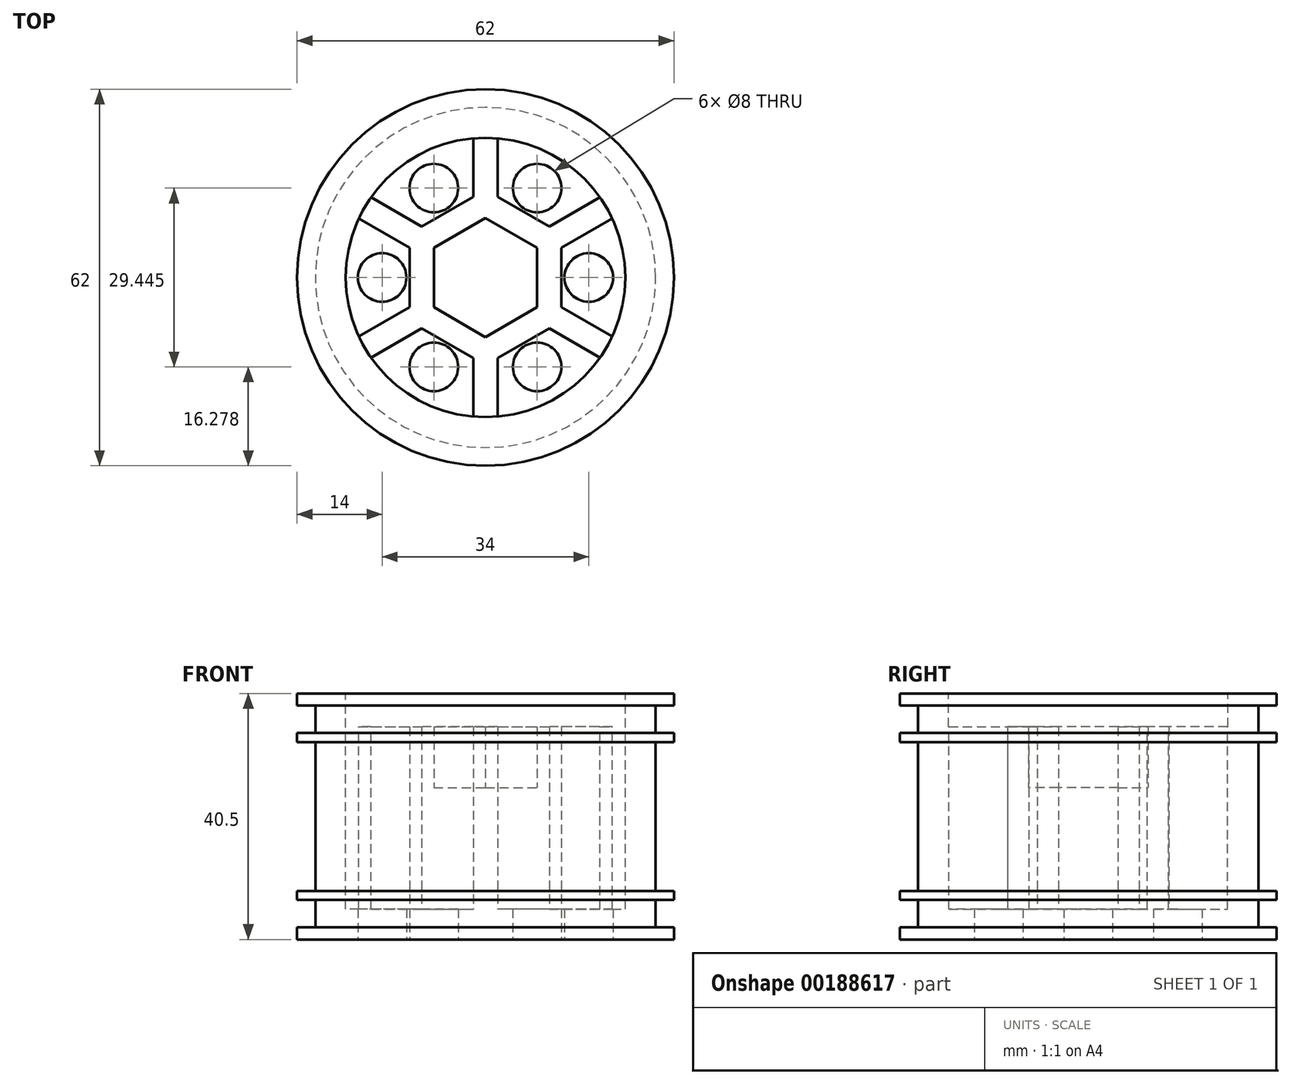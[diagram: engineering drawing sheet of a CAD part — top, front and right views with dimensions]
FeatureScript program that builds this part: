
annotation { "Feature Type Name" : "Feature", "Feature Type Description" : "" }
export const myFeature = defineFeature(function(context is Context, id is Id, definition is map)
    precondition{}
    {
        {
            var Q0;
            Q0=qCreatedBy(makeId("Front.planeOp"),FACE);
            var sketch = newSketch(context, id + "F0", { "sketchPlane" : qUnion([Q0])});
            skLineSegment(sketch, "E0", {"start": v(0, 0) * mm, "end": v(31, 0) * mm});
            skLineSegment(sketch, "E1", {"start": v(31, 0) * mm, "end": v(31, 2) * mm});
            skLineSegment(sketch, "E2", {"start": v(31, 40.5) * mm, "end": v(23, 40.5) * mm});
            skLineSegment(sketch, "E3", {"start": v(0, 5) * mm, "end": v(0, 0) * mm});
            skLineSegment(sketch, "E4.bottom", {"start": v(31, 2) * mm, "end": v(28, 2) * mm});
            skLineSegment(sketch, "E4.top", {"start": v(31, 6.5) * mm, "end": v(28, 6.5) * mm});
            skLineSegment(sketch, "E4.right", {"start": v(28, 2) * mm, "end": v(28, 6.5) * mm});
            skLineSegment(sketch, "E5.bottom", {"start": v(31, 8) * mm, "end": v(28, 8) * mm});
            skLineSegment(sketch, "E5.top", {"start": v(31, 32.5) * mm, "end": v(28, 32.5) * mm});
            skLineSegment(sketch, "E5.right", {"start": v(28, 8) * mm, "end": v(28, 32.5) * mm});
            skLineSegment(sketch, "E6.bottom", {"start": v(31, 38.5) * mm, "end": v(28, 38.5) * mm});
            skLineSegment(sketch, "E6.top", {"start": v(31, 34) * mm, "end": v(28, 34) * mm});
            skLineSegment(sketch, "E6.right", {"start": v(28, 38.5) * mm, "end": v(28, 34) * mm});
            skLineSegment(sketch, "E7.trimOffspring", {"start": v(31, 38.5) * mm, "end": v(31, 40.5) * mm});
            skLineSegment(sketch, "E8.trimOffspring", {"start": v(31, 32.5) * mm, "end": v(31, 34) * mm});
            skLineSegment(sketch, "E9.trimOffspring", {"start": v(31, 6.5) * mm, "end": v(31, 8) * mm});
            skLineSegment(sketch, "E10", {"start": v(23, 40.5) * mm, "end": v(23, 0) * mm});
            skLineSegment(sketch, "E11", {"start": v(0, 5) * mm, "end": v(23, 5) * mm});
            skLineSegment(sketch, "E12", {"start": v(23, 20.25) * mm, "end": v(0, 20.25) * mm});
            skLineSegment(sketch, "E13", {"start": v(23, 40.5) * mm, "end": v(8.5, 20.25) * mm, "construction": true});
            skSolve(sketch);
        }
        {
            var Q0;
            Q0 = qSketchRegion(id + "F0", true);
            var Q1;
            Q1=sQuery(id+"F0.wireOp",EDGE,"E3");
            revolve(context, id + "F1", {"entities" : qUnion([Q0]), "axis" : qUnion([Q1]), "revolveType" : RevolveType.FULL});
        }
        {
            var Q0;
            Q0=makeQuery(id+"F1.opRevolve","SWEPT_FACE",FACE,{"disambiguationData":[OSD([sQuery(id+"F0.wireOp",EDGE,"E0")])]});
            var sketch = newSketch(context, id + "F2", { "sketchPlane" : qUnion([Q0])});
            skCircle(sketch, "E14", {"center": v(-17, 0) * mm, "radius": 4 * mm});
            skCircle(sketch, "E15.1.0", {"center": v(-8.5, -14.72) * mm, "radius": 4 * mm});
            skCircle(sketch, "E15.2.0", {"center": v(8.5, -14.72) * mm, "radius": 4 * mm});
            skCircle(sketch, "E15.3.0", {"center": v(17, 0) * mm, "radius": 4 * mm});
            skCircle(sketch, "E15.4.0", {"center": v(8.5, 14.72) * mm, "radius": 4 * mm});
            skCircle(sketch, "E15.5.0", {"center": v(-8.5, 14.72) * mm, "radius": 4 * mm});
            skPoint(sketch, "E15.center", {"position": v(0, 0) * mm});
            skSolve(sketch);
        }
        {
            var Q0;
            Q0 = qSketchRegion(id + "F2", true);
            var Q1;
            Q1=makeQuery(id+"F1.opRevolve","SWEPT_FACE",FACE,{"disambiguationData":[OSD([sQuery(id+"F0.wireOp",EDGE,"E11")])]});
            extrude(context, id + "F3", {"entities" : qUnion([Q0]), "operationType" : NewBodyOperationType.REMOVE, "endBound" : BoundingType.UP_TO_SURFACE, "oppositeDirection" : true, "endBoundEntityFace" : qUnion([Q1]), "depth" : 25 * mm});
        }
        {
            var Q0;
            Q0=qCreatedBy(makeId("Top.planeOp"),FACE);
            var sketch = newSketch(context, id + "F4", { "sketchPlane" : qUnion([Q0])});
            skCircle(sketch, "E16.cCircle", {"center": v(0, 0) * mm, "radius": 8.5 * mm, "construction": true});
            skLineSegment(sketch, "E16.0", {"start": v(0, 9.81) * mm, "end": v(8.5, 4.9) * mm});
            skLineSegment(sketch, "E16.1", {"start": v(8.5, 4.9) * mm, "end": v(8.5, -4.9) * mm});
            skLineSegment(sketch, "E16.2", {"start": v(8.5, -4.9) * mm, "end": v(0, -9.81) * mm});
            skLineSegment(sketch, "E16.3", {"start": v(0, -9.81) * mm, "end": v(-8.5, -4.9) * mm});
            skLineSegment(sketch, "E16.4", {"start": v(-8.5, -4.9) * mm, "end": v(-8.5, 4.9) * mm});
            skLineSegment(sketch, "E16.5", {"start": v(-8.5, 4.9) * mm, "end": v(0, 9.81) * mm});
            skPoint(sketch, "E16.0.midPoint", {"position": v(4.25, 7.36) * mm});
            skLineSegment(sketch, "E17.bottom", {"start": v(-2, 23) * mm, "end": v(2, 23) * mm});
            skLineSegment(sketch, "E17.top", {"start": v(-2, 9.81) * mm, "end": v(2, 9.81) * mm});
            skLineSegment(sketch, "E17.left", {"start": v(-2, 23) * mm, "end": v(-2, 9.81) * mm});
            skLineSegment(sketch, "E17.right", {"start": v(2, 23) * mm, "end": v(2, 9.81) * mm});
            skPoint(sketch, "E18", {"position": v(0, 23) * mm});
            skLineSegment(sketch, "E19.0", {"start": v(0, -14.43) * mm, "end": v(-12.5, -7.22) * mm});
            skLineSegment(sketch, "E19.1", {"start": v(-12.5, 7.22) * mm, "end": v(0, 14.43) * mm});
            skLineSegment(sketch, "E19.2", {"start": v(0, 14.43) * mm, "end": v(12.5, 7.22) * mm});
            skLineSegment(sketch, "E19.3", {"start": v(-12.5, -7.22) * mm, "end": v(-12.5, 7.22) * mm});
            skLineSegment(sketch, "E19.4", {"start": v(12.5, 7.22) * mm, "end": v(12.5, -7.22) * mm});
            skLineSegment(sketch, "E19.5", {"start": v(12.5, -7.22) * mm, "end": v(0, -14.43) * mm});
            skSolve(sketch);
        }
        {
            var Q0;
            Q0=makeQuery(id+"F4.imprint","IMPRINT",FACE,{"disambiguationData":[TD([[makeQuery(id+"F4.imprint","IMPRINT",EDGE,{"derivedFrom":sQuery(id+"F4.wireOp",EDGE,"E16.0")}),-1.0]])]});
            extrude(context, id + "F6", {"entities" : qUnion([Q0]), "operationType" : NewBodyOperationType.ADD, "depth" : 25 * mm});
        }
        {
            var Q0;
            {var subQ7=sQuery(id+"F4.wireOp",EDGE,"E16.0");Q0=makeQuery(id+"F4.imprint","IMPRINT",FACE,{"disambiguationData":[TD([[makeQuery(id+"F4.imprint","IMPRINT",EDGE,{"derivedFrom":subQ7}),1.0]])]});}
            var Q1;
            {var subQ1=sQuery(id+"F4.wireOp",EDGE,"E17.top");var subQ5=sQuery(id+"F4.wireOp",EDGE,"E17.left");var subQ6=makeQuery(id+"F4.imprint","INTERSECT",VERTEX,{"derivedFrom":[subQ1,subQ5]});Q1=makeQuery(id+"F4.imprint","IMPRINT",FACE,{"disambiguationData":[TD([[makeQuery(id+"F4.imprint","IMPRINT",EDGE,{"disambiguationData":[TD([[subQ6,1.0]])],"derivedFrom":subQ5}),1.0]])]});}
            extrude(context, id + "F7", {"entities" : qUnion([Q0, Q1]), "operationType" : NewBodyOperationType.ADD, "depth" : 35 * mm});
        }
        {
            var Q0;
            {var subQ6=sQuery(id+"F4.wireOp",EDGE,"E17.bottom");Q0=makeQuery(id+"F4.imprint","IMPRINT",FACE,{"disambiguationData":[TD([[makeQuery(id+"F4.imprint","IMPRINT",EDGE,{"derivedFrom":subQ6}),-1.0]])]});}
            extrude(context, id + "F5", {"entities" : qUnion([Q0]), "depth" : 35 * mm});
        }
        {
            var Q0;
            Q0=makeQuery(id+"F5.opExtrude","SWEPT_BODY",BODY,{"disambiguationData":[OSD([sQuery(id+"F4.wireOp",EDGE,"E17.bottom"),sQuery(id+"F4.wireOp",EDGE,"E17.left"),sQuery(id+"F4.wireOp",EDGE,"E17.right"),sQuery(id+"F4.wireOp",EDGE,"E19.1"),sQuery(id+"F4.wireOp",EDGE,"E19.2")])]});
            var Q1;
            Q1=makeQuery(id+"F1.opRevolve","SWEPT_EDGE",EDGE,{"disambiguationData":[OSD([sQuery(id+"F0.wireOp",EDGE,"E2"),sQuery(id+"F0.wireOp",EDGE,"E10")])]});
            circularPattern(context, id + "F8", {"operationType" : NewBodyOperationType.ADD, "entities" : qUnion([Q0]), "axis" : qUnion([Q1]), "angle" : 360 * degree, "instanceCount" : 6, "equalSpace" : true});
        }
    });
